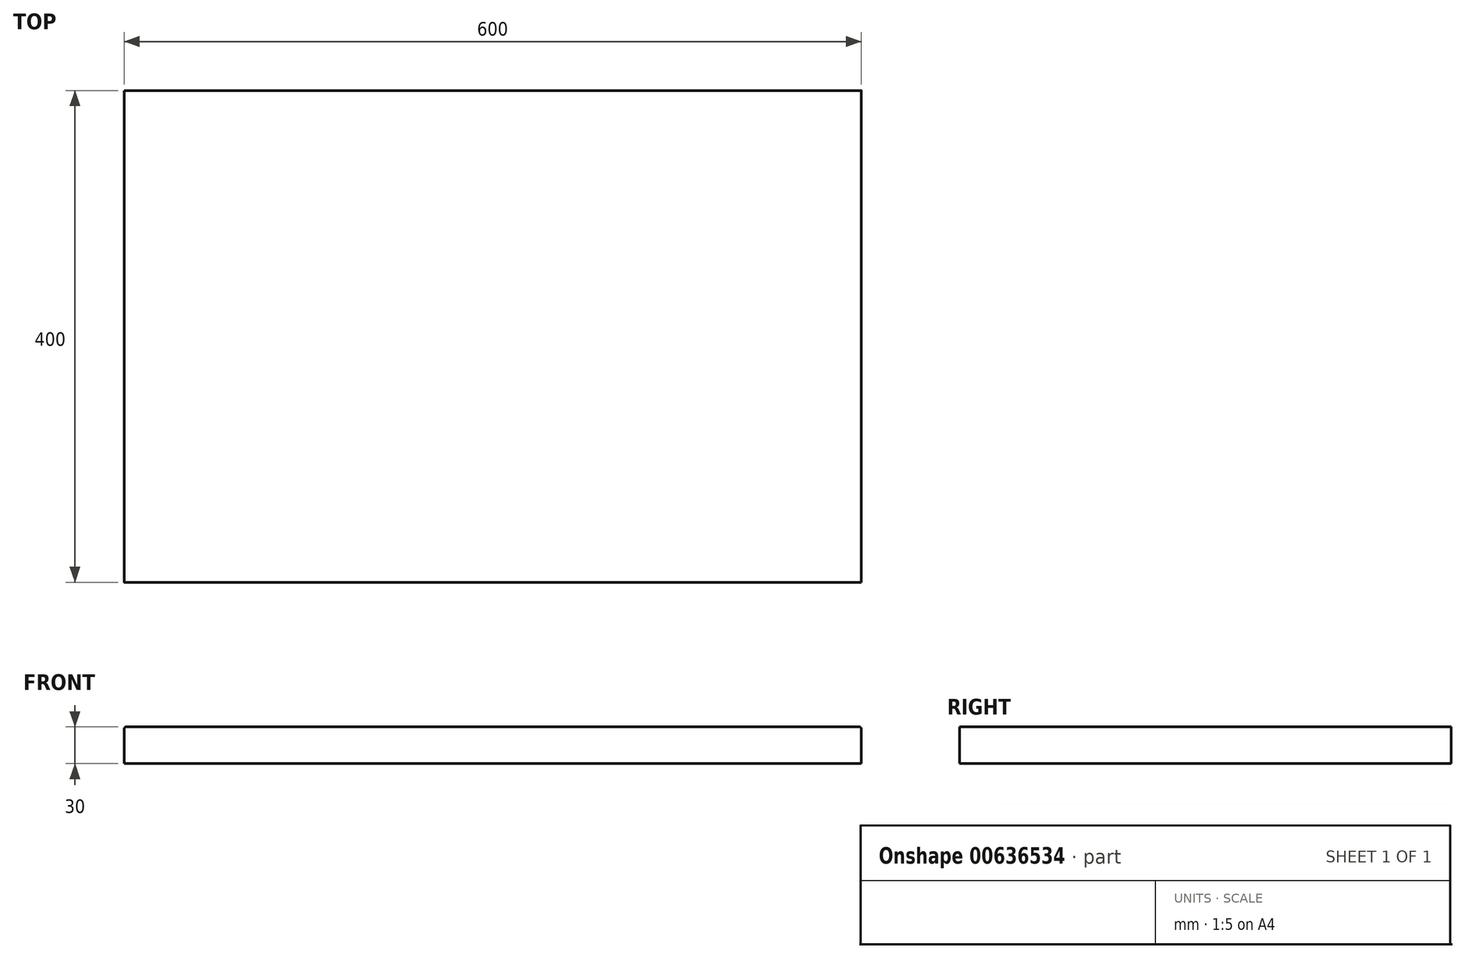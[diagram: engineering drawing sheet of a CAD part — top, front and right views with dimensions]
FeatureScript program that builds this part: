
annotation { "Feature Type Name" : "Feature", "Feature Type Description" : "" }
export const myFeature = defineFeature(function(context is Context, id is Id, definition is map)
    precondition{}
    {
        {
            var Q0;
            Q0=qCreatedBy(makeId("Front.planeOp"),FACE);
            var sketch = newSketch(context, id + "F0", { "sketchPlane" : qUnion([Q0])});
            skLineSegment(sketch, "E0.bottom", {"start": v(-300, 15) * mm, "end": v(300, 15) * mm});
            skLineSegment(sketch, "E0.top", {"start": v(-300, -15) * mm, "end": v(300, -15) * mm});
            skLineSegment(sketch, "E0.left", {"start": v(-300, 15) * mm, "end": v(-300, -15) * mm});
            skLineSegment(sketch, "E0.right", {"start": v(300, 15) * mm, "end": v(300, -15) * mm});
            skPoint(sketch, "E0.middle", {"position": v(0, 0) * mm});
            skSolve(sketch);
        }
        {
            var Q0;
            Q0=makeQuery(id+"F0.imprint","IMPRINT",FACE,{"disambiguationData":[TD([[makeQuery(id+"F0.imprint","IMPRINT",EDGE,{"derivedFrom":sQuery(id+"F0.wireOp",EDGE,"E0.bottom")}),-1.0]])]});
            extrude(context, id + "F1", {"entities" : qUnion([Q0]), "depth" : 400 * mm, "offsetDistance" : 25 * mm});
        }
        {
            var Q0;
            Q0=makeQuery(id+"F1.opExtrude","SWEPT_EDGE",EDGE,{"disambiguationData":[OSD([sQuery(id+"F0.wireOp",EDGE,"E0.bottom"),sQuery(id+"F0.wireOp",EDGE,"E0.right")])]});
            var Q1;
            Q1=makeQuery(id+"F1.opExtrude","SWEPT_EDGE",EDGE,{"disambiguationData":[OSD([sQuery(id+"F0.wireOp",EDGE,"E0.bottom"),sQuery(id+"F0.wireOp",EDGE,"E0.left")])]});
            fillet(context, id + "F2", {"entities" : qUnion([Q0, Q1]), "radius" : 2 * mm, "tangentPropagation" : true, "allowEdgeOverflow" : false});
        }
    });
